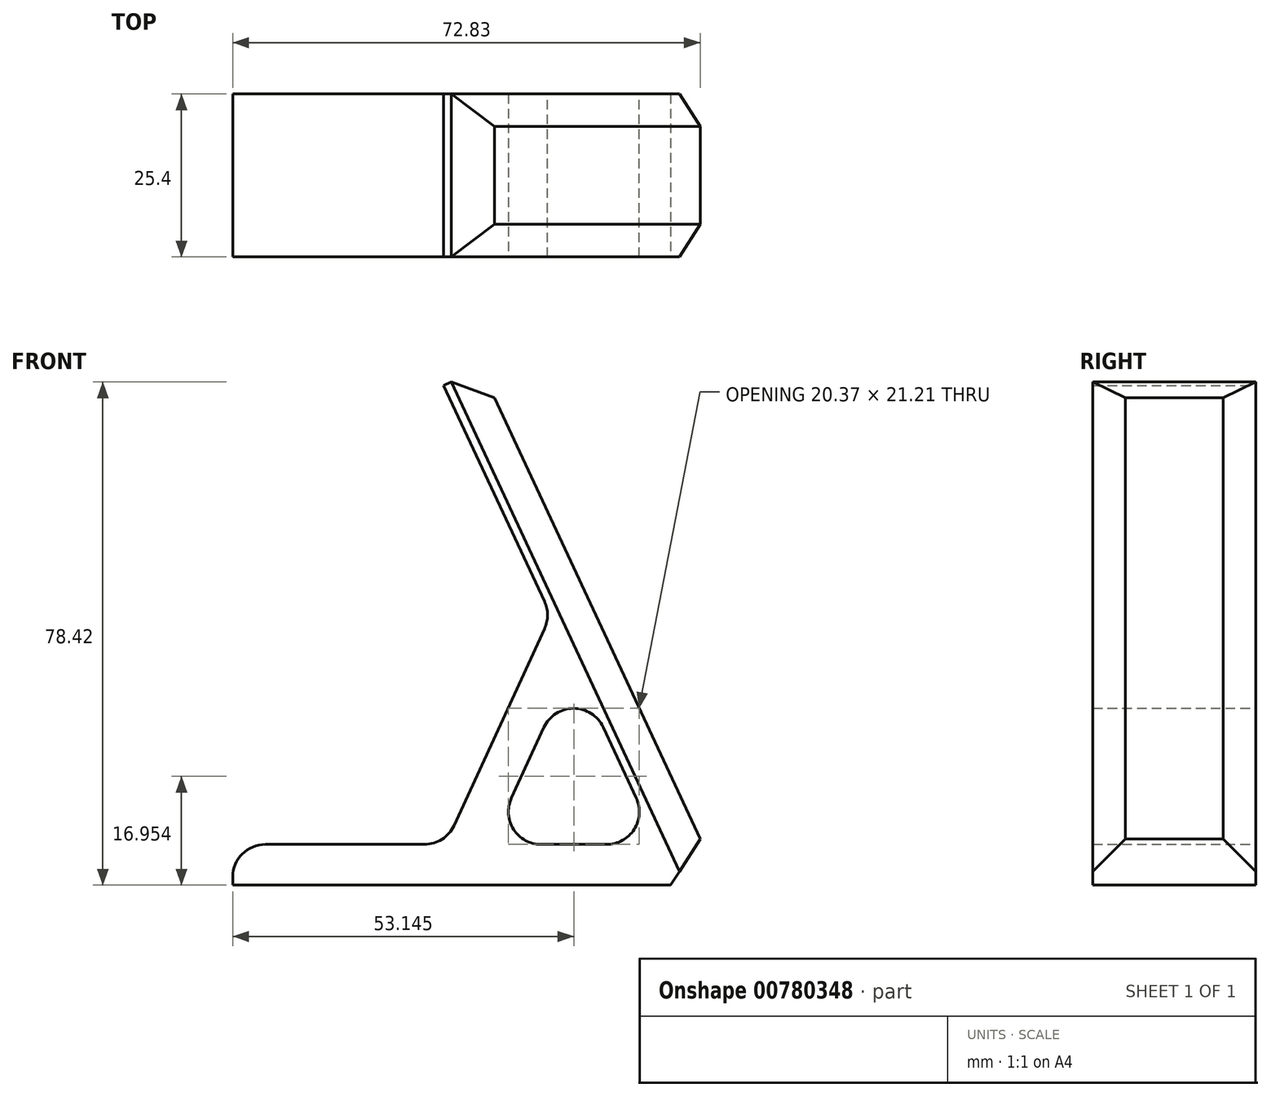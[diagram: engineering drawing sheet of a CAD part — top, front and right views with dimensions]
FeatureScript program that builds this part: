
annotation { "Feature Type Name" : "Feature", "Feature Type Description" : "" }
export const myFeature = defineFeature(function(context is Context, id is Id, definition is map)
    precondition{}
    {
        {
            var Q0;
            Q0=qCreatedBy(makeId("Front.planeOp"),FACE);
            var sketch = newSketch(context, id + "F0", { "sketchPlane" : qUnion([Q0])});
            skLineSegment(sketch, "E0", {"start": v(0, 0) * mm, "end": v(-76.2, 0) * mm});
            skLineSegment(sketch, "E1", {"start": v(0, 0) * mm, "end": v(-37.57, 80.57) * mm});
            skLineSegment(sketch, "E2.0", {"start": v(-9.97, 6.35) * mm, "end": v(-43.33, 77.89) * mm});
            skLineSegment(sketch, "E2.1", {"start": v(-9.97, 6.35) * mm, "end": v(-76.2, 6.35) * mm});
            skLineSegment(sketch, "E3", {"start": v(-76.2, 6.35) * mm, "end": v(-76.2, 0) * mm});
            skLineSegment(sketch, "E4", {"start": v(-43.33, 77.89) * mm, "end": v(-37.57, 80.57) * mm});
            skLineSegment(sketch, "E5", {"start": v(-26.65, 42.12) * mm, "end": v(-43.08, 6.35) * mm});
            skLineSegment(sketch, "E6", {"start": v(-36.1, 6.35) * mm, "end": v(-23.13, 34.57) * mm});
            skSolve(sketch);
        }
        {
            var Q0;
            Q0=makeQuery(id+"F0.imprint","IMPRINT",FACE,{"disambiguationData":[TD([[makeQuery(id+"F0.imprint","IMPRINT",EDGE,{"derivedFrom":sQuery(id+"F0.wireOp",EDGE,"E0")}),-1.0]])]});
            var Q1;
            {var subQ0=sQuery(id+"F0.wireOp",EDGE,"E5");Q1=makeQuery(id+"F0.imprint","IMPRINT",FACE,{"disambiguationData":[TD([[makeQuery(id+"F0.imprint","IMPRINT",EDGE,{"derivedFrom":subQ0}),1.0]])]});}
            extrude(context, id + "F1", {"entities" : qUnion([Q0, Q1]), "depth" : 25.4 * mm, "offsetDistance" : 25.4 * mm});
        }
        {
            var Q0;
            Q0=makeQuery(id+"F1.opExtrude","SWEPT_FACE",FACE,{"disambiguationData":[OSD([sQuery(id+"F0.wireOp",EDGE,"E1")])]});
            chamfer(context, id + "F2", {"entities" : qUnion([Q0]), "width" : 5.08 * mm, "tangentPropagation" : true});
        }
        {
            var Q0;
            Q0=makeQuery(id+"F1.opExtrude","SWEPT_EDGE",EDGE,{"disambiguationData":[OSD([sQuery(id+"F0.wireOp",EDGE,"E2.0"),sQuery(id+"F0.wireOp",EDGE,"E2.1")])]});
            var Q1;
            Q1=makeQuery(id+"F1.opExtrude","SWEPT_EDGE",EDGE,{"disambiguationData":[OSD([sQuery(id+"F0.wireOp",EDGE,"E2.1"),sQuery(id+"F0.wireOp",EDGE,"E6")])]});
            var Q2;
            Q2=makeQuery(id+"F1.opExtrude","SWEPT_EDGE",EDGE,{"disambiguationData":[OSD([sQuery(id+"F0.wireOp",EDGE,"E2.0"),sQuery(id+"F0.wireOp",EDGE,"E6")])]});
            var Q3;
            Q3=makeQuery(id+"F1.opExtrude","SWEPT_EDGE",EDGE,{"disambiguationData":[OSD([sQuery(id+"F0.wireOp",EDGE,"E2.1"),sQuery(id+"F0.wireOp",EDGE,"E5")])]});
            var Q4;
            Q4=makeQuery(id+"F1.opExtrude","SWEPT_EDGE",EDGE,{"disambiguationData":[OSD([sQuery(id+"F0.wireOp",EDGE,"E2.0"),sQuery(id+"F0.wireOp",EDGE,"E5")])]});
            var Q5;
            Q5=makeQuery(id+"F1.opExtrude","SWEPT_EDGE",EDGE,{"disambiguationData":[OSD([sQuery(id+"F0.wireOp",EDGE,"E2.1"),sQuery(id+"F0.wireOp",EDGE,"E3")])]});
            fillet(context, id + "F3", {"entities" : qUnion([Q0, Q1, Q2, Q3, Q4, Q5]), "radius" : 5.08 * mm, "tangentPropagation" : true, "allowEdgeOverflow" : false});
        }
    });
